# Revit family: Shower-Shower_Trim-KOHLER-Loure-K-T14664
name_source: partatom
category: Plumbing Fixtures
revit_build: Autodesk Revit 2015 (Build: 20140606_1530(x64)
units: mm (PartAtom-declared; Revit-internal decimal feet)

## types (6) — shared parameters
ADA Compliant = No
Assembly Code = D2010700
CW Connection = No
Cold Water Inlet = Cold Water Inlet
Date Modified = 03/22/2019
Drain Included = No
HW Connection = Yes
Height = 6 1/4"
Length = 0"
Manufacturer = KOHLER Co.
MasterFormat 1995 = 15410
MasterFormat 2004 = 22.41.23
Material = Premium Material Construction
Panel Thickness = 0"
Product Documentation Link = https://www.us.kohler.com
Product Name = Loure
Product Page URL = http://www.us.kohler.com
Tempered Water Inlet 1 = Tempered Water Inlet 1
Tempered Water Inlet 2 = Tempered Water Inlet 2
Type Comments = Tempered Water Inlet
URL = https://www.us.kohler.com
Vent Connection = No
Waste Connection = No
Waste Water Outlet = Waste Water Outlet
WaterSense Certified = No
Width = 6 1/4"

## per-type parameters (varying)
| type | Default Elevation | Description | Finish | Model | Type | With_Shower_Head |
| Without Shower Head, CP-Polished Chrome | 42" | Rite-Temp bath and shower trim set with push-button diverter, less showerhead | Kohler-Metal-CP-Polished_Chrome | K-T14664-4L-CP | 4 | No |
| Without Shower Head, SN-Vibrant Polished Nickel | 48" | Rite-Temp bath and shower trim set with push-button diverter, less showerhead | Kohler-Metal-SN-Vibrant_Polished_Nickel | K-T14664-4L-SN | 5 | No |
| Without Shower Head, BN-Vibrant Brushed Nickel | 42" | Rite-Temp bath and shower trim set with push-button diverter, less showerhead | Kohler-Metal-BN-Vibrant_Brushed_Nickel | K-T14664-4L-BN | 6 | No |
| With Shower Head, CP-Polished Chrome | 42" | Rite-Temp bath/shower trim set | Kohler-Metal-CP-Polished_Chrome | K-T14664-4-CP | 1 | Yes |
| With Shower Head, BN-Vibrant Brushed Nickel | 42" | Rite-Temp bath/shower trim set | Kohler-Metal-BN-Vibrant_Brushed_Nickel | K-T14664-4-BN | 3 | Yes |
| With Shower Head, SN-Vibrant Polished Nickel | 42" | Rite-Temp bath/shower trim set | Kohler-Metal-BN-Vibrant_Brushed_Nickel | K-T14664-4-SN | 2 | Yes |

## geometry (parser evidence)
native form markers: Sweep x14
no freeform markers — native parametric forms only
